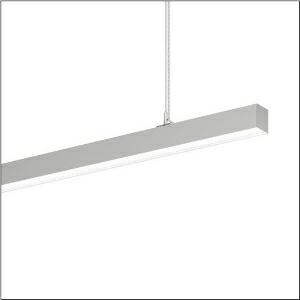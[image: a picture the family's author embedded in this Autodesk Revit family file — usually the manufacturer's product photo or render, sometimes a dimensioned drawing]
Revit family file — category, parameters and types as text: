
# Revit family: silica_r__21_51mx30tct9s_9c67
name_source: partatom
category: Lighting Fixtures
units: mm (PartAtom-declared; Revit-internal decimal feet)

## family parameters
Cut with Voids When Loaded = No
Host = Face
Light Source = No
Part Type = Normal
Room Calculation Point = No
Round Connector Dimension = Use Diameter
Shared = No

## types (1)
- --- (1 x LED, 10300 lm, 84.4 W, 6500K)
    Apparent Load = 84 VA
    CIE Flux Codes = 47 79 96 58 100
    Color Rendering = 80
    Color Temperature = 6500K
    Default Elevation = 1800 mm
    Description = Silica® 21, office luminaire, primary optical cover: cover, of PMMA, opal, light emission: direct/indirect distribution, primary light characteristic: symmetric, installation type: suspended mounting, LED, rated luminous flux: 10.300lm, luminous efficacy: 116lm/W, light colour: 8tw, colour temperature: 2700..6500K, control gear: ECG DALI, with terminal, 3+2-pole, max. 2.5mm², mains connection: 220..240V, AC, 50/60Hz, rated input power: 88.7W, luminaire housing, of aluminium, metallic grey (RAL 9006), length: 3.004mm, width: 53mm, height: 53mm, protection rating (complete): IP20, insulation class (complete): insulation class I (protective earthing), certification: CE, permissible operating ambient temperature: 0..+35°C, standard: EN 50419, packaging unit: 1 piece
    Height = 53 mm
    Lamp = 1 x LED
    Lamp Light Flux = 10300 lm
    Lamp Power = 84.4 W
    Lamp count = 1
    Length = 3004 mm
    Luminous efficacy = 122 lm/W
    Manufacturer = Siteco
    ModVariant = No
    Model = 51MX30TCT9S
    Mounting Place = Ceiling
    Mounting Type = Pendant
    Number of Poles = 1
    OnlyDefault = Yes
    Power Factor = 1
    Product Name = Silica® 21
    Product group = office luminaire | ceiling pendant
    ProductGroupID = 905
    Protection Class = Protection class I
    Protection Degree = IP 20
    RLX_Detail_Level = 1
    RlxData = <blob elided: 20053 chars, md5=31bb6336>
    Socket = socket
    Standby Power = 0 W
    System Light Flux = 10300 lm
    System Power = 84 W
    Type Comments = individual setting
    Type Image = l_1251727.jpg
    URL = http://relux.com
    VarID = @adj_045699
    Voltage = 0 V
    Weight = 0.00 kg
    Width = 53 mm

## geometry (parser evidence)
native form markers: Blend x4, Sweep x11
no freeform markers — native parametric forms only
